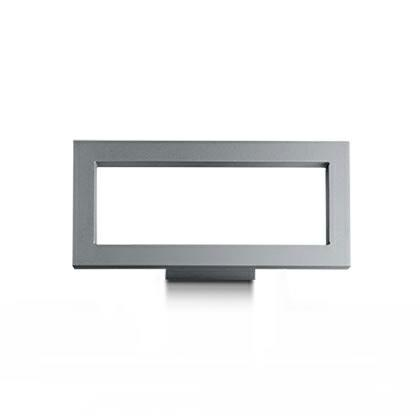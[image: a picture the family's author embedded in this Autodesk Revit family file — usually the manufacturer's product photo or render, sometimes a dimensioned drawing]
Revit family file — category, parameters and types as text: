
# Revit family: SIMES_S.3171W_Trim Applique
name_source: partatom
category: Lighting Fixtures
revit_build: Autodesk Revit 2016 (Build: 20150714_1515(x64)
units: mm (PartAtom-declared; Revit-internal decimal feet)

## family parameters
Cut with Voids When Loaded = No
Host = Face
Light Source = Yes
OmniClass Number = 23.80.70.14
OmniClass Title = Luminaries for External Lighting
Part Type = Normal
Room Calculation Point = No
Round Connector Dimension = Use Diameter
Shared = No

## types (1)
- SIMES_S.3171W_Trim Applique
    Approval mark = CE, ENEC
    Assembly Code = D5020
    BIMobject category = Outside
    Brand url = http://www.simes.it
    Color Filter = 16777215
    Color Rendering Index = CRI 90
    Colour Temperature = 3000
    Control Gear = electronic transformer
    Default Elevation = 1219 mm
    Description = TRIM RECTANGULAR APPLIQUE
Art. S.3171W
MODULES LED 3000K  230V CRI 90 MacAdam step 3
Rated luminaire luminous flux: 1270lm
Rated input power: 18W
Luminaire efficacy: 71lm/W
Electronic ballast 220÷230V 50/60Hz
CE - ENEC 03

PRODUCT TYPE
Wall mounted luminaire. Bollard fitting ( bollard version ). IP rating IP 54
MATERIAL CHARACTERISTICS
Aluminium die cast housing in EN AB-47100 (low copper content) with high resistance against corrosion. Extruded EN AW-6060 aluminium structure (bollard version) with high corrosion resistance. Stone wash surface treatment prior to painting process. A4 grade Stainless Steel screws with 2,5-3% molybdenum content which increases the resistance against corrosion. Silicone gaskets. Painting Process : 3 Step Process
1) Surface treatment with BONDERITE. A heavy metal free chemical surface treatment containing ceramic nano particles giving a cohesive, inorganic and highly dense protective coating. 2) PRE POLYMERIZATION a process of introducing an epoxy primer with excellent characteristics to the paint which also offers very high resistance to oxidation due to its Zinc content. 3) POLYMERIZATION a process with the application of polyester powder with high resistance against UV rays and harsh weather conditions. Resistance test protection for Marine applications for 1200h.  Mechanical resistance IK 09
LIGHTING PERFORMANCE
Toughened glass diffuser 4mm thick. LOR --. Trim double emission has been developed to ensure maximum visual comfort. The direct light of the front side is diffused by a special glass, to prevents glare and avoid the visibility of the LEDs. The indirect light is evenly distributed on the wall thanks to a second diffusing glass positioned on the rear side of the luminaire. Colour rendering index  CRI 90, Colour stability step  MacAdam step 3. 
WIRING
Hard wired with H07RN-F cable 1,0m. Isolation: CLASS I . Available colours: White (cod.01), Aluminium grey (cod.14). Weight: 0.6 Kg Glow Wire test: --
Lamp included.
TRIM REGISTERED DESIGN
This luminaire contains built-in LED modules with energy class: A, A+, A++. In case of damage or malfunction please contact the manufacturer to receive additional instructions on how to replace and relative spare parts to order. The LED modules cannot be handled in the luminaire by the end user (Regulation UE 874/2012).
LED circuit boards are engineered accordingly to actual Lumen Maintenance regulation (LM80) and Technical Memorandum (TM21) where uniformity and quality of light is 50.000 hours referred to L70  B20 Ta 25°C.Lifecycle refers to LED circuit boards only, all others components of the luminaire are excluded.
    Design country = Italy
    Dimming Lamp Color Temperature Shift = <None>
    Edition number = 1
    Frequency = 50/60Hz
    IFC Classification = Light Fixture
    IK Rating = IK 06
    Installation instructions = http://www.simes.it
    Lamp = LED
    Lamp Light Flux = 1800
    Lamp count = 1
    Last Update = 08/11/2018 17:18:37
    Lifetime = 50000 L70 B20 Ta 25°C
    Light Output Ratio = 100
    Luminous efficacy = 70,6
    Manufacturer = SIMES
    Manufacturer country = Italy
    Manufacturer name = Simes
    Masterformat 2014 Code = 26 56 00
    Masterformat 2014 Description = Exterior Lighting
    Material main = Aluminium
    Material secondary = Glass
    Model = S.3171W
    Mounting Place = Wall
    Mounting Type = Surface mounted
    NBS Reference Code = 49
    NBS Reference Description = Luminaries And Lamps
    Nominal height = 17000
    Nominal width = 17000
    OmniClass Code = 23-35 47 11
    OmniClass Description = Lighting Fixture
    Photometric Web File = S3171W.ies
    Product Group = wall-mounted luminaire
    Product Guid = 5eed9a8a-40da-4078-8ecc-114165e49aca
    Product Name = Trim Applique
    Product SKU = TRIM
    Product certification = http://www.simes.it
    Product data url = https://bimobject.com
    Product url = http://www.simes.it
    Protection Class = Protection class I
    Protection Degree = IP 54
    QR code = http://bimobject.com
    System Light Flux = 1270
    System Power = 18
    Technical description = http://www.simes.it
    Tilt Angle = 90.00°
    Type Comments = SIMES S.p.A. - All rights reserved
    Type Image = trim-applique-rect.jpg
    UNSPSC Code = 3911
    URL = http://www.simes.it
    Uniclass 1.4 Code = YJ73
    Uniclass 1.4 Description = Luminaries and lamps
    Uniclass 2.0 Code = PR-49
    Uniclass 2.0 Description = Luminaries and lamps
    Uniclass 2015 Code = EF_70_80
    Uniclass 2015 Name = Lighting
    Uniformat II Code = D5020
    Uniformat II Description = Lighting & Branch Wiring
    Voltage = 220÷230V
    Weight Net (Kg) = 1

## geometry (parser evidence)
native form markers: Blend x4
no freeform markers — native parametric forms only
